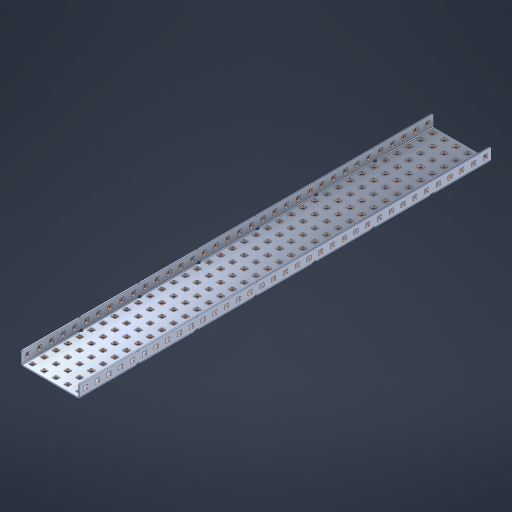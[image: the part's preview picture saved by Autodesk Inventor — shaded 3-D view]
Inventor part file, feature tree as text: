
AUTODESK INVENTOR PART (.ipt)
format: ipt  version: 2023 (Build 270158000, 158)  size: 2,540,544 bytes
history: native  units: in
note: dims shown in document units (in); Inventor stores cm internally (conversion verified against a paired STEP export)
features: other x250, extrude x244, sheet_metal_op x10, sketch x8, mirror x1, pattern_linear x1, chamfer x1
ambient origin geometry x8: Origin, YZ Plane, XZ Plane, XY Plane, X Axis, Y Axis, Z Axis, Center Point
bodies: Solid1 (feature_tree), Body (feature_tree)
feature tree (515):
  other  "Flange Pattern Plane"
  sheet_metal_op  "Flange Pattern"
  sheet_metal_op  "Body Pattern"
  other  "Arc Length"
  mirror  "Notch Mirror"
  pattern_linear  "Notch Pattern"  Spacing1=0.1875in  [1 undecoded]
  chamfer  "End Chamfer"
  extrude  "Half Cut"  Depth=0.0469in
  sketch  "Sketch1"  dims[d0=2.5in]
  other  "Plate1"
  sketch  "Sketch2"  dims[d1=17.5in]
  other  "Plate2"
  sheet_metal_op  "Bend1"
  sheet_metal_op  "Corner1"
  sketch  "Sketch3"  dims[d2=0.0469in]
  other  "Flange Pattern Sketch"
  sketch  "Sketch7"  dims[d3=0.0469in]
  other  "Srf1"
  other  "Srf2"
  sketch  "Sketch8"  dims[d4=0.0234in]
  sketch  "Sketch9"  dims[d5=0.0938in]
  other  "Srf91"
  sheet_metal_op  "Body Pattern Sketch"
  other  "Srf92"
  sketch  "Sketch13"  dims[d6=0.0469in]
  sketch  "Sketch14"  dims[d7=0.5in d8=90.0deg d9=0.0312in d10=0.1875in d11=0.0469in d12=0.0469in d16=0.182in d17=0.02in d18=0.0469in d19=0.0in d20=0.25in d21=0.25in d46=0.172in d47=1.0in d48=0.0in d49=0.182in d50=0.02in d51=0.25in d52=0.25in d53=0.0469in d54=0.0in d55=0.172in d56=1.0in d57=0.0in d60=13.7795in d62=0.5in d63=1.9685in d65=0.5in d85=0.1227in d86=0.1659in d88=0.04in d89=0.0469in d90=0.0in d91=0.04in d92=0.0491in d95=2.5in d96=0.04in d97=0.25in d98=45.0deg d101=0.0in d102=2.497in d131=2.5in d132=13.7795in d134=0.5in d139=0.5in]
  other  "Srf856"
  other  "Srf1310"
  other  "Srf1311"
  other  "Srf1312"
  other  "Srf1376"
  other  "Srf1377"
  other  "Srf1728"
  other  "Srf1755"
  other  "Srf1878"
  other  "Srf1879"
  other  "Srf1880"
  other  "Srf1881"
  other  "Srf1882"
  other  "Srf1883"
  other  "Srf1884"
  other  "Srf1885"
  other  "Srf1886"
  other  "Srf1887"
  other  "Srf1888"
  other  "Srf1889"
  other  "Srf1890"
  other  "Srf1891"
  other  "Srf1892"
  other  "Srf1893"
  other  "Srf1894"
  other  "Srf1895"
  other  "Srf1896"
  other  "Srf1897"
  other  "Srf1898"
  other  "Srf1899"
  other  "Srf1900"
  other  "Srf1901"
  other  "Srf1902"
  other  "Srf1903"
  other  "Srf1904"
  other  "Srf1905"
  other  "Srf1906"
  other  "Srf1942"
  other  "Srf1943"
  other  "Srf1944"
  other  "Srf1945"
  other  "Srf1946"
  other  "Srf1947"
  other  "Srf1948"
  other  "Srf1949"
  other  "Srf1950"
  other  "Srf1951"
  other  "Srf1952"
  other  "Srf1953"
  other  "Srf1954"
  other  "Srf1955"
  other  "Srf1956"
  other  "Srf1957"
  other  "Srf1958"
  other  "Srf1959"
  other  "Srf1960"
  other  "Srf1961"
  other  "Srf1962"
  other  "Srf1963"
  other  "Srf1964"
  other  "Srf1965"
  other  "Srf1966"
  other  "Srf1967"
  other  "Srf1968"
  other  "Srf1969"
  other  "Srf1970"
  other  "Srf2111"
  other  "Srf2112"
  other  "Srf2113"
  other  "Srf2114"
  other  "Srf2115"
  other  "Srf2116"
  other  "Srf2117"
  other  "Srf2118"
  other  "Srf2119"
  other  "Srf2120"
  other  "Srf2121"
  other  "Srf2122"
  other  "Srf2123"
  other  "Srf2124"
  other  "Srf2125"
  other  "Srf2126"
  other  "Srf2127"
  other  "Srf2128"
  other  "Srf2129"
  other  "Srf2130"
  other  "Srf2131"
  other  "Srf2132"
  other  "Srf2133"
  other  "Srf2134"
  other  "Srf2135"
  other  "Srf2136"
  other  "Srf2137"
  other  "Srf2138"
  other  "Srf2139"
  other  "Srf2140"
  other  "Srf2141"
  other  "Srf2142"
  other  "Srf2143"
  other  "Srf2144"
  other  "Srf2145"
  other  "Srf2146"
  other  "Srf2147"
  other  "Srf2148"
  other  "Srf2149"
  other  "Srf2150"
  other  "Srf2151"
  other  "Srf2152"
  other  "Srf2153"
  other  "Srf2154"
  other  "Srf2155"
  other  "Srf2156"
  other  "Srf2157"
  other  "Srf2158"
  other  "Srf2159"
  other  "Srf2160"
  other  "Srf2161"
  other  "Srf2162"
  other  "Srf2163"
  other  "Srf2164"
  other  "Srf2165"
  other  "Srf2166"
  other  "Srf2167"
  other  "Srf2168"
  other  "Srf2169"
  other  "Srf2170"
  other  "Srf2171"
  other  "Srf2172"
  other  "Srf2173"
  other  "Srf2174"
  other  "Srf2175"
  other  "Srf2176"
  other  "Srf2177"
  other  "Srf2178"
  other  "Srf2179"
  other  "Srf2180"
  other  "Srf2181"
  other  "Srf2182"
  other  "Srf2183"
  other  "Srf2184"
  other  "Srf2185"
  other  "Srf2186"
  other  "Srf2187"
  other  "Srf2188"
  other  "Srf2189"
  other  "Srf2190"
  other  "Srf2191"
  other  "Srf2192"
  other  "Srf2193"
  other  "Srf2194"
  other  "Srf2195"
  other  "Srf2196"
  other  "Srf2197"
  other  "Srf2198"
  other  "Srf2199"
  other  "Srf2200"
  other  "Srf2201"
  other  "Srf2202"
  other  "Srf2203"
  other  "Srf2204"
  other  "Srf2205"
  other  "Srf2206"
  other  "Srf2207"
  other  "Srf2208"
  other  "Srf2209"
  other  "Srf2210"
  other  "Srf2211"
  other  "Srf2212"
  other  "Srf2213"
  other  "Srf2214"
  other  "Srf2215"
  other  "Srf2216"
  other  "Srf2217"
  other  "Srf2218"
  other  "Srf2219"
  other  "Srf2220"
  other  "Srf2221"
  other  "Srf2222"
  other  "Srf2223"
  other  "Srf2224"
  other  "Srf2225"
  other  "Srf2226"
  other  "Srf2227"
  other  "Srf2228"
  other  "Srf2229"
  other  "Srf2230"
  other  "Srf2231"
  other  "Srf2232"
  other  "Srf2233"
  other  "Srf2234"
  other  "Srf2235"
  other  "Srf2236"
  other  "Srf2237"
  other  "Srf2238"
  other  "Srf2239"
  other  "Srf2240"
  other  "Srf2241"
  other  "Srf2242"
  other  "Srf2243"
  other  "Srf2244"
  other  "Srf2245"
  other  "Srf2246"
  other  "Srf2247"
  other  "Srf2248"
  other  "Srf2249"
  other  "Srf2250"
  other  "Srf2251"
  other  "Srf2252"
  other  "Srf2253"
  other  "Srf2254"
  other  "Srf2255"
  other  "Srf2256"
  other  "Srf2257"
  other  "Srf2258"
  other  "Srf2259"
  other  "Srf2260"
  other  "Srf2261"
  other  "Srf2262"
  other  "Srf2263"
  other  "Srf2264"
  other  "Srf2265"
  other  "Srf2266"
  other  "Srf2267"
  other  "Srf2268"
  other  "Srf2269"
  other  "Srf2270"
  other  "Srf2271"
  other  "Srf2272"
  other  "Srf2273"
  other  "Srf2274"
  other  "Srf2275"
  other  "Srf2276"
  other  "Srf2277"
  other  "Srf2278"
  other  "Srf2279"
  other  "Srf2280"
  other  "Srf2281"
  other  "Srf2282"
  other  "Srf2283"
  other  "Srf2284"
  other  "Srf2285"
  sheet_metal_op  "Flange Stamp"
  sheet_metal_op  "Flange Circle"
  sheet_metal_op  "Body Stamp"
  sheet_metal_op  "Body Circle"
  sheet_metal_op  "Notch"
  extrude  "ExtrusionSrf2"  Depth=0.0469in
  extrude  "ExtrusionSrf92"  Depth=2.5in
  extrude  "ExtrusionSrf856"  Depth=0.02in
  extrude  "ExtrusionSrf1310"  Depth=0.0469in
  extrude  "ExtrusionSrf1311"  TaperAngle=0.0deg  [1 undecoded]
  extrude  "ExtrusionSrf1312"  Depth=0.25in
  extrude  "ExtrusionSrf1376"  Depth=0.25in
  extrude  "ExtrusionSrf1377"  Depth=2.5in
  extrude  "ExtrusionSrf1728"  Depth=2.5in TaperAngle=0.0deg
  extrude  "ExtrusionSrf1755"  Depth=2.5in
  extrude  "ExtrusionSrf1878"  Depth=0.02in
  extrude  "ExtrusionSrf1879"  Depth=0.25in
  extrude  "ExtrusionSrf1880"  Depth=0.25in
  extrude  "ExtrusionSrf1881"  Depth=0.0469in
  extrude  "ExtrusionSrf1882"  TaperAngle=0.0deg  [1 undecoded]
  extrude  "ExtrusionSrf1883"  Depth=2.5in
  extrude  "ExtrusionSrf1884"  Depth=2.5in TaperAngle=0.0deg
  extrude  "ExtrusionSrf1885"  Depth=2.5in
  extrude  "ExtrusionSrf1886"  Depth=2.5in
  extrude  "ExtrusionSrf1887"  Depth=2.5in
  extrude  "ExtrusionSrf1888"  Depth=2.5in
  extrude  "ExtrusionSrf1889"  Depth=2.5in
  extrude  "ExtrusionSrf1890"  Depth=0.0469in
  extrude  "ExtrusionSrf1891"  TaperAngle=0.0deg  [1 undecoded]
  extrude  "ExtrusionSrf1892"  Depth=2.5in
  extrude  "ExtrusionSrf1893"  Depth=2.5in
  extrude  "ExtrusionSrf1894"  Depth=2.5in
  extrude  "ExtrusionSrf1895"  Depth=0.25in TaperAngle=45.0deg
  extrude  "ExtrusionSrf1896"  TaperAngle=0.0deg  [1 undecoded]
  extrude  "ExtrusionSrf1897"  Depth=2.5in
  extrude  "ExtrusionSrf1898"  Depth=2.5in
  extrude  "ExtrusionSrf1899"  Depth=2.5in
  extrude  "ExtrusionSrf1900"  Depth=2.5in
  extrude  "ExtrusionSrf1901"  Depth=2.5in
  extrude  "ExtrusionSrf1902"  [1 undecoded]
  extrude  "ExtrusionSrf1903"  [1 undecoded]
  extrude  "ExtrusionSrf1904"  [1 undecoded]
  extrude  "ExtrusionSrf1905"  [1 undecoded]
  extrude  "ExtrusionSrf1906"  [1 undecoded]
  extrude  "ExtrusionSrf1942"  [1 undecoded]
  extrude  "ExtrusionSrf1943"  [1 undecoded]
  extrude  "ExtrusionSrf1944"  [1 undecoded]
  extrude  "ExtrusionSrf1945"  [1 undecoded]
  extrude  "ExtrusionSrf1946"  [1 undecoded]
  extrude  "ExtrusionSrf1947"  [1 undecoded]
  extrude  "ExtrusionSrf1948"  [1 undecoded]
  extrude  "ExtrusionSrf1949"  [1 undecoded]
  extrude  "ExtrusionSrf1950"  [1 undecoded]
  extrude  "ExtrusionSrf1951"  [1 undecoded]
  extrude  "ExtrusionSrf1952"  [1 undecoded]
  extrude  "ExtrusionSrf1953"  [1 undecoded]
  extrude  "ExtrusionSrf1954"  [1 undecoded]
  extrude  "ExtrusionSrf1955"  [1 undecoded]
  extrude  "ExtrusionSrf1956"  [1 undecoded]
  extrude  "ExtrusionSrf1957"  [1 undecoded]
  extrude  "ExtrusionSrf1958"  [1 undecoded]
  extrude  "ExtrusionSrf1959"  [1 undecoded]
  extrude  "ExtrusionSrf1960"  [1 undecoded]
  extrude  "ExtrusionSrf1961"  [1 undecoded]
  extrude  "ExtrusionSrf1962"  [1 undecoded]
  extrude  "ExtrusionSrf1963"  [1 undecoded]
  extrude  "ExtrusionSrf1964"  [1 undecoded]
  extrude  "ExtrusionSrf1965"  [1 undecoded]
  extrude  "ExtrusionSrf1966"  [1 undecoded]
  extrude  "ExtrusionSrf1967"  [1 undecoded]
  extrude  "ExtrusionSrf1968"  [1 undecoded]
  extrude  "ExtrusionSrf1969"  [1 undecoded]
  extrude  "ExtrusionSrf1970"  [1 undecoded]
  extrude  "ExtrusionSrf2111"  [1 undecoded]
  extrude  "ExtrusionSrf2112"  [1 undecoded]
  extrude  "ExtrusionSrf2113"  [1 undecoded]
  extrude  "ExtrusionSrf2114"  [1 undecoded]
  extrude  "ExtrusionSrf2115"  [1 undecoded]
  extrude  "ExtrusionSrf2116"  [1 undecoded]
  extrude  "ExtrusionSrf2117"  [1 undecoded]
  extrude  "ExtrusionSrf2118"  [1 undecoded]
  extrude  "ExtrusionSrf2119"  [1 undecoded]
  extrude  "ExtrusionSrf2120"  [1 undecoded]
  extrude  "ExtrusionSrf2121"  [1 undecoded]
  extrude  "ExtrusionSrf2122"  [1 undecoded]
  extrude  "ExtrusionSrf2123"  [1 undecoded]
  extrude  "ExtrusionSrf2124"  [1 undecoded]
  extrude  "ExtrusionSrf2125"  [1 undecoded]
  extrude  "ExtrusionSrf2126"  [1 undecoded]
  extrude  "ExtrusionSrf2127"  [1 undecoded]
  extrude  "ExtrusionSrf2128"  [1 undecoded]
  extrude  "ExtrusionSrf2129"  [1 undecoded]
  extrude  "ExtrusionSrf2130"  [1 undecoded]
  extrude  "ExtrusionSrf2131"  [1 undecoded]
  extrude  "ExtrusionSrf2132"  [1 undecoded]
  extrude  "ExtrusionSrf2133"  [1 undecoded]
  extrude  "ExtrusionSrf2134"  [1 undecoded]
  extrude  "ExtrusionSrf2135"  [1 undecoded]
  extrude  "ExtrusionSrf2136"  [1 undecoded]
  extrude  "ExtrusionSrf2137"  [1 undecoded]
  extrude  "ExtrusionSrf2138"  [1 undecoded]
  extrude  "ExtrusionSrf2139"  [1 undecoded]
  extrude  "ExtrusionSrf2140"  [1 undecoded]
  extrude  "ExtrusionSrf2141"  [1 undecoded]
  extrude  "ExtrusionSrf2142"  [1 undecoded]
  extrude  "ExtrusionSrf2143"  [1 undecoded]
  extrude  "ExtrusionSrf2144"  [1 undecoded]
  extrude  "ExtrusionSrf2145"  [1 undecoded]
  extrude  "ExtrusionSrf2146"  [1 undecoded]
  extrude  "ExtrusionSrf2147"  [1 undecoded]
  extrude  "ExtrusionSrf2148"  [1 undecoded]
  extrude  "ExtrusionSrf2149"  [1 undecoded]
  extrude  "ExtrusionSrf2150"  [1 undecoded]
  extrude  "ExtrusionSrf2151"  [1 undecoded]
  extrude  "ExtrusionSrf2152"  [1 undecoded]
  extrude  "ExtrusionSrf2153"  [1 undecoded]
  extrude  "ExtrusionSrf2154"  [1 undecoded]
  extrude  "ExtrusionSrf2155"  [1 undecoded]
  extrude  "ExtrusionSrf2156"  [1 undecoded]
  extrude  "ExtrusionSrf2157"  [1 undecoded]
  extrude  "ExtrusionSrf2158"  [1 undecoded]
  extrude  "ExtrusionSrf2159"  [1 undecoded]
  extrude  "ExtrusionSrf2160"  [1 undecoded]
  extrude  "ExtrusionSrf2161"  [1 undecoded]
  extrude  "ExtrusionSrf2162"  [1 undecoded]
  extrude  "ExtrusionSrf2163"  [1 undecoded]
  extrude  "ExtrusionSrf2164"  [1 undecoded]
  extrude  "ExtrusionSrf2165"  [1 undecoded]
  extrude  "ExtrusionSrf2166"  [1 undecoded]
  extrude  "ExtrusionSrf2167"  [1 undecoded]
  extrude  "ExtrusionSrf2168"  [1 undecoded]
  extrude  "ExtrusionSrf2169"  [1 undecoded]
  extrude  "ExtrusionSrf2170"  [1 undecoded]
  extrude  "ExtrusionSrf2171"  [1 undecoded]
  extrude  "ExtrusionSrf2172"  [1 undecoded]
  extrude  "ExtrusionSrf2173"  [1 undecoded]
  extrude  "ExtrusionSrf2174"  [1 undecoded]
  extrude  "ExtrusionSrf2175"  [1 undecoded]
  extrude  "ExtrusionSrf2176"  [1 undecoded]
  extrude  "ExtrusionSrf2177"  [1 undecoded]
  extrude  "ExtrusionSrf2178"  [1 undecoded]
  extrude  "ExtrusionSrf2179"  [1 undecoded]
  extrude  "ExtrusionSrf2180"  [1 undecoded]
  extrude  "ExtrusionSrf2181"  [1 undecoded]
  extrude  "ExtrusionSrf2182"  [1 undecoded]
  extrude  "ExtrusionSrf2183"  [1 undecoded]
  extrude  "ExtrusionSrf2184"  [1 undecoded]
  extrude  "ExtrusionSrf2185"  [1 undecoded]
  extrude  "ExtrusionSrf2186"  [1 undecoded]
  extrude  "ExtrusionSrf2187"  [1 undecoded]
  extrude  "ExtrusionSrf2188"  [1 undecoded]
  extrude  "ExtrusionSrf2189"  [1 undecoded]
  extrude  "ExtrusionSrf2190"  [1 undecoded]
  extrude  "ExtrusionSrf2191"  [1 undecoded]
  extrude  "ExtrusionSrf2192"  [1 undecoded]
  extrude  "ExtrusionSrf2193"  [1 undecoded]
  extrude  "ExtrusionSrf2194"  [1 undecoded]
  extrude  "ExtrusionSrf2195"  [1 undecoded]
  extrude  "ExtrusionSrf2196"  [1 undecoded]
  extrude  "ExtrusionSrf2197"  [1 undecoded]
  extrude  "ExtrusionSrf2198"  [1 undecoded]
  extrude  "ExtrusionSrf2199"  [1 undecoded]
  extrude  "ExtrusionSrf2200"  [1 undecoded]
  extrude  "ExtrusionSrf2201"  [1 undecoded]
  extrude  "ExtrusionSrf2202"  [1 undecoded]
  extrude  "ExtrusionSrf2203"  [1 undecoded]
  extrude  "ExtrusionSrf2204"  [1 undecoded]
  extrude  "ExtrusionSrf2205"  [1 undecoded]
  extrude  "ExtrusionSrf2206"  [1 undecoded]
  extrude  "ExtrusionSrf2207"  [1 undecoded]
  extrude  "ExtrusionSrf2208"  [1 undecoded]
  extrude  "ExtrusionSrf2209"  [1 undecoded]
  extrude  "ExtrusionSrf2210"  [1 undecoded]
  extrude  "ExtrusionSrf2211"  [1 undecoded]
  extrude  "ExtrusionSrf2212"  [1 undecoded]
  extrude  "ExtrusionSrf2213"  [1 undecoded]
  extrude  "ExtrusionSrf2214"  [1 undecoded]
  extrude  "ExtrusionSrf2215"  [1 undecoded]
  extrude  "ExtrusionSrf2216"  [1 undecoded]
  extrude  "ExtrusionSrf2217"  [1 undecoded]
  extrude  "ExtrusionSrf2218"  [1 undecoded]
  extrude  "ExtrusionSrf2219"  [1 undecoded]
  extrude  "ExtrusionSrf2220"  [1 undecoded]
  extrude  "ExtrusionSrf2221"  [1 undecoded]
  extrude  "ExtrusionSrf2222"  [1 undecoded]
  extrude  "ExtrusionSrf2223"  [1 undecoded]
  extrude  "ExtrusionSrf2224"  [1 undecoded]
  extrude  "ExtrusionSrf2225"  [1 undecoded]
  extrude  "ExtrusionSrf2226"  [1 undecoded]
  extrude  "ExtrusionSrf2227"  [1 undecoded]
  extrude  "ExtrusionSrf2228"  [1 undecoded]
  extrude  "ExtrusionSrf2229"  [1 undecoded]
  extrude  "ExtrusionSrf2230"  [1 undecoded]
  extrude  "ExtrusionSrf2231"  [1 undecoded]
  extrude  "ExtrusionSrf2232"  [1 undecoded]
  extrude  "ExtrusionSrf2233"  [1 undecoded]
  extrude  "ExtrusionSrf2234"  [1 undecoded]
  extrude  "ExtrusionSrf2235"  [1 undecoded]
  extrude  "ExtrusionSrf2236"  [1 undecoded]
  extrude  "ExtrusionSrf2237"  [1 undecoded]
  extrude  "ExtrusionSrf2238"  [1 undecoded]
  extrude  "ExtrusionSrf2239"  [1 undecoded]
  extrude  "ExtrusionSrf2240"  [1 undecoded]
  extrude  "ExtrusionSrf2241"  [1 undecoded]
  extrude  "ExtrusionSrf2242"  [1 undecoded]
  extrude  "ExtrusionSrf2243"  [1 undecoded]
  extrude  "ExtrusionSrf2244"  [1 undecoded]
  extrude  "ExtrusionSrf2245"  [1 undecoded]
  extrude  "ExtrusionSrf2246"  [1 undecoded]
  extrude  "ExtrusionSrf2247"  [1 undecoded]
  extrude  "ExtrusionSrf2248"  [1 undecoded]
  extrude  "ExtrusionSrf2249"  [1 undecoded]
  extrude  "ExtrusionSrf2250"  [1 undecoded]
  extrude  "ExtrusionSrf2251"  [1 undecoded]
  extrude  "ExtrusionSrf2252"  [1 undecoded]
  extrude  "ExtrusionSrf2253"  [1 undecoded]
  extrude  "ExtrusionSrf2254"  [1 undecoded]
  extrude  "ExtrusionSrf2255"  [1 undecoded]
  extrude  "ExtrusionSrf2256"  [1 undecoded]
  extrude  "ExtrusionSrf2257"  [1 undecoded]
  extrude  "ExtrusionSrf2258"  [1 undecoded]
  extrude  "ExtrusionSrf2259"  [1 undecoded]
  extrude  "ExtrusionSrf2260"  [1 undecoded]
  extrude  "ExtrusionSrf2261"  [1 undecoded]
  extrude  "ExtrusionSrf2262"  [1 undecoded]
  extrude  "ExtrusionSrf2263"  [1 undecoded]
  extrude  "ExtrusionSrf2264"  [1 undecoded]
  extrude  "ExtrusionSrf2265"  [1 undecoded]
  extrude  "ExtrusionSrf2266"  [1 undecoded]
  extrude  "ExtrusionSrf2267"  [1 undecoded]
  extrude  "ExtrusionSrf2268"  [1 undecoded]
  extrude  "ExtrusionSrf2269"  [1 undecoded]
  extrude  "ExtrusionSrf2270"  [1 undecoded]
  extrude  "ExtrusionSrf2271"  [1 undecoded]
  extrude  "ExtrusionSrf2272"  [1 undecoded]
  extrude  "ExtrusionSrf2273"  [1 undecoded]
  extrude  "ExtrusionSrf2274"  [1 undecoded]
  extrude  "ExtrusionSrf2275"  [1 undecoded]
  extrude  "ExtrusionSrf2276"  [1 undecoded]
  extrude  "ExtrusionSrf2277"  [1 undecoded]
  extrude  "ExtrusionSrf2278"  [1 undecoded]
  extrude  "ExtrusionSrf2279"  [1 undecoded]
  extrude  "ExtrusionSrf2280"  [1 undecoded]
  extrude  "ExtrusionSrf2281"  [1 undecoded]
  extrude  "ExtrusionSrf2282"  [1 undecoded]
  extrude  "ExtrusionSrf2283"  [1 undecoded]
  extrude  "ExtrusionSrf2284"  [1 undecoded]
  extrude  "ExtrusionSrf2285"  [1 undecoded]
note: 214 required parameter values undecoded (feature->parameter linkage not recoverable at this tier; creation-order binding heuristic only, values carry confidence <= 0.55)
